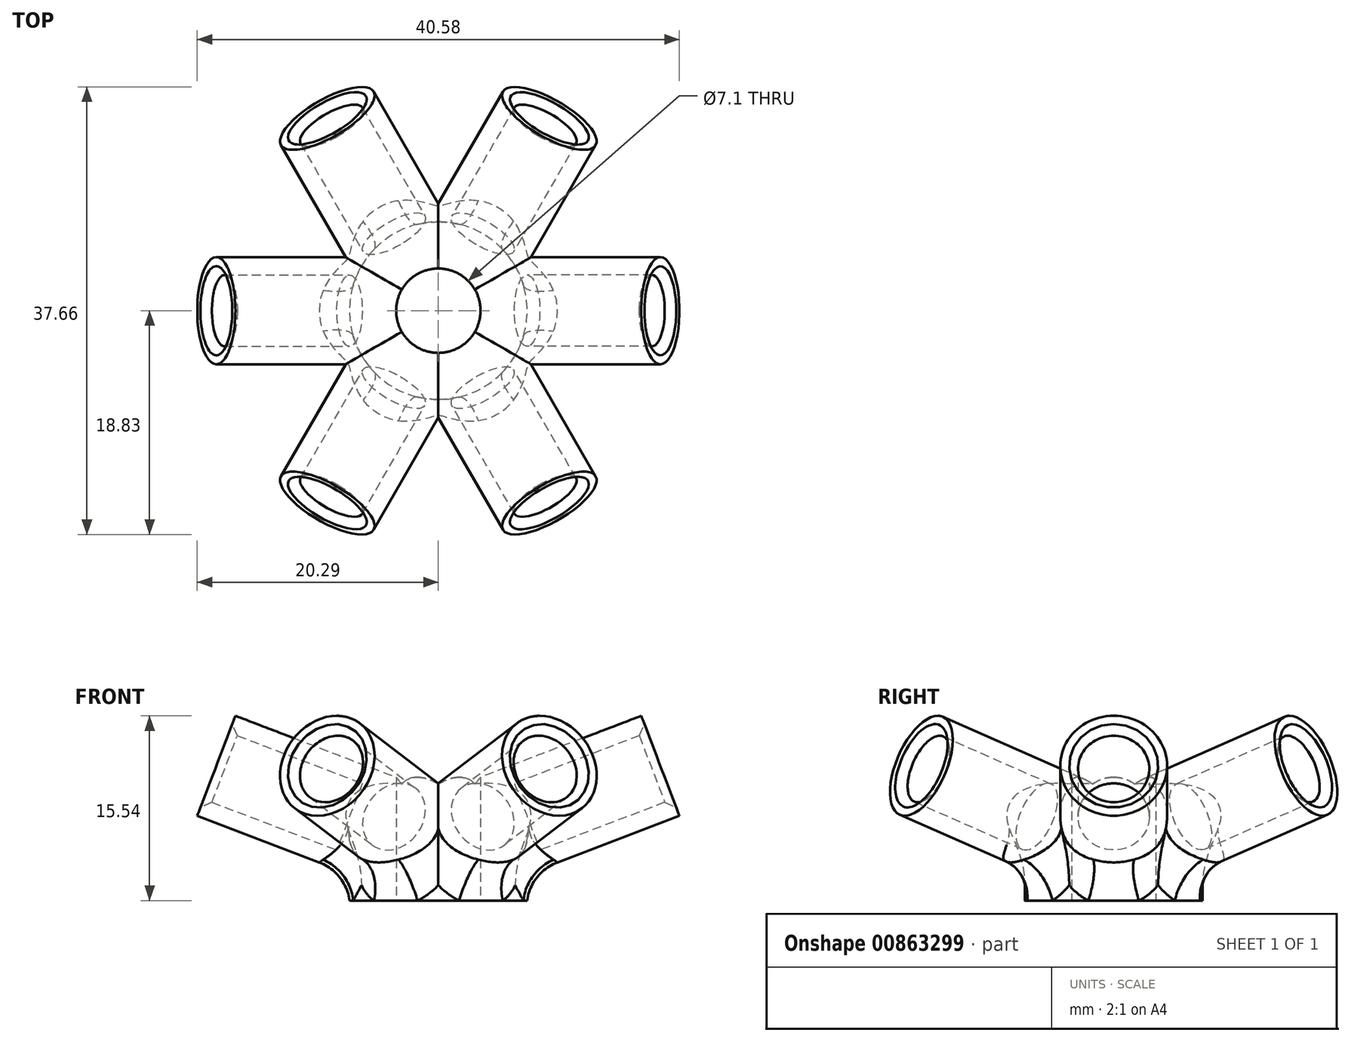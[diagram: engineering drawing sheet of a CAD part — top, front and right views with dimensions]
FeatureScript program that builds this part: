
annotation { "Feature Type Name" : "Feature", "Feature Type Description" : "" }
export const myFeature = defineFeature(function(context is Context, id is Id, definition is map)
    precondition{}
    {
        {
            assignVariable(context, id + "F0", {"name" : "espesor", "anyValue" : 1.5});
        }
        {
            var Q0;
            Q0=qCreatedBy(makeId("Front.planeOp"),FACE);
            var sketch = newSketch(context, id + "F1", { "sketchPlane" : qUnion([Q0])});
            skLineSegment(sketch, "E0", {"start": v(0, 0) * mm, "end": v(18.68, 7.14) * mm, "construction": true});
            skLineSegment(sketch, "E1", {"start": v(0, 0) * mm, "end": v(1.6, -4.2) * mm});
            skLineSegment(sketch, "E2", {"start": v(18.68, 7.14) * mm, "end": v(20.29, 2.93) * mm});
            skLineSegment(sketch, "E3", {"start": v(1.6, -4.2) * mm, "end": v(20.29, 2.93) * mm});
            skLineSegment(sketch, "E4", {"start": v(19.75, 4.33) * mm, "end": v(8.54, 0.05) * mm});
            skLineSegment(sketch, "E5", {"start": v(8.54, 0.05) * mm, "end": v(7.47, 2.85) * mm});
            skLineSegment(sketch, "E6", {"start": v(7.47, 2.85) * mm, "end": v(0, 0) * mm});
            skLineSegment(sketch, "E7", {"start": v(0, 0) * mm, "end": v(0, 41.35) * mm, "construction": true});
            skLineSegment(sketch, "E8", {"start": v(1.6, -4.2) * mm, "end": v(0, -4.2) * mm, "construction": true});
            skLineSegment(sketch, "E9", {"start": v(7.47, 2.85) * mm, "end": v(7.47, -4.2) * mm, "construction": true});
            skLineSegment(sketch, "E10", {"start": v(7.47, -4.2) * mm, "end": v(1.6, -4.2) * mm, "construction": true});
            skLineSegment(sketch, "E11", {"start": v(0, -4.2) * mm, "end": v(7.47, -4.2) * mm});
            skLineSegment(sketch, "E12", {"start": v(7.47, -4.2) * mm, "end": v(7.47, 2.85) * mm});
            skLineSegment(sketch, "E13", {"start": v(0, 2.85) * mm, "end": v(7.47, 2.85) * mm});
            skLineSegment(sketch, "E14", {"start": v(0, 2.85) * mm, "end": v(0, -4.2) * mm});
            skSolve(sketch);
        }
        {
            var Q0;
            {var subQ1=sQuery(id+"F1.wireOp",EDGE,"E4");Q0=makeQuery(id+"F1.imprint","IMPRINT",FACE,{"disambiguationData":[TD([[makeQuery(id+"F1.imprint","IMPRINT",EDGE,{"derivedFrom":subQ1}),1.0]])]});}
            var Q1;
            {var subQ0=sQuery(id+"F1.wireOp",EDGE,"E1");Q1=makeQuery(id+"F1.imprint","IMPRINT",FACE,{"disambiguationData":[TD([[makeQuery(id+"F1.imprint","IMPRINT",EDGE,{"derivedFrom":subQ0}),1.0]])]});}
            var Q2;
            Q2=sQuery(id+"F1.wireOp",EDGE,"E0");
            revolve(context, id + "F2", {"surfaceOperationType" : NewSurfaceOperationType.NEW, "entities" : qUnion([Q0, Q1]), "axis" : qUnion([Q2]), "revolveType" : RevolveType.FULL});
        }
        {
            var Q0;
            Q0=makeQuery(id+"F2.opRevolve","SWEPT_BODY",BODY,{"disambiguationData":[OSD([sQuery(id+"F1.wireOp",EDGE,"E1"),sQuery(id+"F1.wireOp",EDGE,"E2"),sQuery(id+"F1.wireOp",EDGE,"E3"),sQuery(id+"F1.wireOp",EDGE,"E4"),sQuery(id+"F1.wireOp",EDGE,"E5"),sQuery(id+"F1.wireOp",EDGE,"E6")])]});
            var Q1;
            Q1=sQuery(id+"F1.wireOp",EDGE,"E7");
            circularPattern(context, id + "F3", {"operationType" : NewBodyOperationType.ADD, "entities" : qUnion([Q0]), "axis" : qUnion([Q1]), "angle" : 360 * degree, "instanceCount" : 6, "equalSpace" : true});
        }
        {
            var Q0;
            {var subQ0=sQuery(id+"F1.wireOp",EDGE,"E1");Q0=makeQuery(id+"F1.imprint","IMPRINT",FACE,{"disambiguationData":[TD([[makeQuery(id+"F1.imprint","IMPRINT",EDGE,{"derivedFrom":subQ0}),-1.0]])]});}
            var Q1;
            {var subQ0=sQuery(id+"F1.wireOp",EDGE,"E1");Q1=makeQuery(id+"F1.imprint","IMPRINT",FACE,{"disambiguationData":[TD([[makeQuery(id+"F1.imprint","IMPRINT",EDGE,{"derivedFrom":subQ0}),1.0]])]});}
            var Q2;
            {var subQ0=sQuery(id+"F1.wireOp",EDGE,"E11");var subQ3=sQuery(id+"F1.wireOp",EDGE,"E12");var subQ5=makeQuery(id+"F1.imprint","INTERSECT",VERTEX,{"derivedFrom":[subQ0,subQ3]});Q2=makeQuery(id+"F1.imprint","IMPRINT",FACE,{"disambiguationData":[TD([[makeQuery(id+"F1.imprint","IMPRINT",EDGE,{"disambiguationData":[TD([[subQ5,-1.0]])],"derivedFrom":subQ3}),1.0]])]});}
            var Q3;
            {var subQ0=sQuery(id+"F1.wireOp",EDGE,"E6");Q3=makeQuery(id+"F1.imprint","IMPRINT",FACE,{"disambiguationData":[TD([[makeQuery(id+"F1.imprint","IMPRINT",EDGE,{"derivedFrom":subQ0}),-1.0]])]});}
            var Q4;
            Q4=sQuery(id+"F1.wireOp",EDGE,"E13");
            var Q5;
            Q5=sQuery(id+"F1.wireOp",EDGE,"E14");
            var Q6;
            Q6=sQuery(id+"F1.wireOp",EDGE,"E7");
            revolve(context, id + "F4", {"surfaceOperationType" : NewSurfaceOperationType.NEW, "entities" : qUnion([Q0, Q1, Q2, Q3]), "surfaceEntities" : qUnion([Q4, Q5]), "axis" : qUnion([Q6]), "revolveType" : RevolveType.FULL});
        }
        {
            var Q0;
            Q0=makeQuery(id+"F4.opRevolve","SWEPT_FACE",FACE,{"disambiguationData":[OSD([sQuery(id+"F1.wireOp",EDGE,"E11")])]});
            var sketch = newSketch(context, id + "F5", { "sketchPlane" : qUnion([Q0])});
            skCircle(sketch, "E15", {"center": v(0, 0) * mm, "radius": 3.55 * mm});
            skSolve(sketch);
        }
        {
            var Q0;
            Q0=makeQuery(id+"F5.imprint","IMPRINT",FACE,{"disambiguationData":[TD([[makeQuery(id+"F5.imprint","IMPRINT",EDGE,{"derivedFrom":sQuery(id+"F5.wireOp",EDGE,"E15")}),1.0]])]});
            extrude(context, id + "F6", {"entities" : qUnion([Q0]), "operationType" : NewBodyOperationType.REMOVE, "endBound" : BoundingType.THROUGH_ALL, "oppositeDirection" : true, "depth" : 25 * mm, "offsetDistance" : 25 * mm});
        }
        {
            var Q0;
            Q0=makeQuery(id+"F2.opRevolve","SWEPT_BODY",BODY,{"disambiguationData":[OSD([sQuery(id+"F1.wireOp",EDGE,"E1"),sQuery(id+"F1.wireOp",EDGE,"E2"),sQuery(id+"F1.wireOp",EDGE,"E3"),sQuery(id+"F1.wireOp",EDGE,"E4"),sQuery(id+"F1.wireOp",EDGE,"E5"),sQuery(id+"F1.wireOp",EDGE,"E6")])]});
            var Q1;
            Q1=makeQuery(id+"F4.opRevolve","SWEPT_BODY",BODY,{"disambiguationData":[OSD([sQuery(id+"F1.wireOp",EDGE,"E11"),sQuery(id+"F1.wireOp",EDGE,"E12"),sQuery(id+"F1.wireOp",EDGE,"E13"),sQuery(id+"F1.wireOp",EDGE,"E14")])]});
            booleanBodies(context, id + "F7", {"operationType" : BooleanOperationType.UNION, "tools" : qUnion([Q0, Q1])});
        }
        {
            var Q0;
            {var subQ0=makeQuery(id+"F2.opRevolve","SWEPT_FACE",FACE,{"disambiguationData":[OSD([sQuery(id+"F1.wireOp",EDGE,"E1")])]});var subQ1=makeQuery(id+"F2.opRevolve","SWEPT_FACE",FACE,{"disambiguationData":[OSD([sQuery(id+"F1.wireOp",EDGE,"E3")])]});Q0=makeQuery(id+"F7.opBoolean","INTERSECT",EDGE,{"derivedFrom":[makeQuery(id+"F4.opRevolve","SWEPT_FACE",FACE,{"disambiguationData":[OSD([sQuery(id+"F1.wireOp",EDGE,"E12")])]}),makeQuery(id+"F3.boolean.opBoolean","SPLIT",FACE,{"disambiguationData":[TD([subQ0])],"derivedFrom":makeQuery(id+"F3.opPattern","COPY",FACE,{"derivedFrom":subQ1,"instanceName":"1"})})]});}
            var Q1;
            {var subQ0=makeQuery(id+"F2.opRevolve","SWEPT_FACE",FACE,{"disambiguationData":[OSD([sQuery(id+"F1.wireOp",EDGE,"E3")])]});Q1=makeQuery(id+"F7.opBoolean","INTERSECT",EDGE,{"derivedFrom":[makeQuery(id+"F4.opRevolve","SWEPT_FACE",FACE,{"disambiguationData":[OSD([sQuery(id+"F1.wireOp",EDGE,"E12")])]}),makeQuery(id+"F3.boolean.opBoolean","SPLIT",FACE,{"disambiguationData":[TD([subQ0])],"derivedFrom":makeQuery(id+"F3.opPattern","COPY",FACE,{"derivedFrom":subQ0,"instanceName":"2"})})]});}
            var Q2;
            {var subQ0=makeQuery(id+"F2.opRevolve","SWEPT_FACE",FACE,{"disambiguationData":[OSD([sQuery(id+"F1.wireOp",EDGE,"E3")])]});var subQ1=makeQuery(id+"F2.opRevolve","SWEPT_FACE",FACE,{"disambiguationData":[OSD([sQuery(id+"F1.wireOp",EDGE,"E1")])]});Q2=makeQuery(id+"F7.opBoolean","INTERSECT",EDGE,{"derivedFrom":[makeQuery(id+"F4.opRevolve","SWEPT_FACE",FACE,{"disambiguationData":[OSD([sQuery(id+"F1.wireOp",EDGE,"E12")])]}),makeQuery(id+"F3.boolean.opBoolean","SPLIT",FACE,{"disambiguationData":[TD([subQ1])],"derivedFrom":subQ0})]});}
            var Q3;
            {var subQ0=makeQuery(id+"F2.opRevolve","SWEPT_FACE",FACE,{"disambiguationData":[OSD([sQuery(id+"F1.wireOp",EDGE,"E3")])]});var subQ1=makeQuery(id+"F2.opRevolve","SWEPT_FACE",FACE,{"disambiguationData":[OSD([sQuery(id+"F1.wireOp",EDGE,"E1")])]});Q3=makeQuery(id+"F7.opBoolean","INTERSECT",EDGE,{"derivedFrom":[makeQuery(id+"F4.opRevolve","SWEPT_FACE",FACE,{"disambiguationData":[OSD([sQuery(id+"F1.wireOp",EDGE,"E12")])]}),makeQuery(id+"F3.boolean.opBoolean","SPLIT",FACE,{"disambiguationData":[TD([subQ1])],"derivedFrom":makeQuery(id+"F3.opPattern","COPY",FACE,{"derivedFrom":subQ0,"instanceName":"5"})})]});}
            var Q4;
            {var subQ1=makeQuery(id+"F2.opRevolve","SWEPT_FACE",FACE,{"disambiguationData":[OSD([sQuery(id+"F1.wireOp",EDGE,"E3")])]});Q4=makeQuery(id+"F7.opBoolean","INTERSECT",EDGE,{"derivedFrom":[makeQuery(id+"F4.opRevolve","SWEPT_FACE",FACE,{"disambiguationData":[OSD([sQuery(id+"F1.wireOp",EDGE,"E12")])]}),makeQuery(id+"F3.boolean.opBoolean","SPLIT",FACE,{"disambiguationData":[TD([subQ1])],"derivedFrom":makeQuery(id+"F3.opPattern","COPY",FACE,{"derivedFrom":subQ1,"instanceName":"4"})})]});}
            var Q5;
            {var subQ1=makeQuery(id+"F2.opRevolve","SWEPT_FACE",FACE,{"disambiguationData":[OSD([sQuery(id+"F1.wireOp",EDGE,"E3")])]});Q5=makeQuery(id+"F7.opBoolean","INTERSECT",EDGE,{"derivedFrom":[makeQuery(id+"F4.opRevolve","SWEPT_FACE",FACE,{"disambiguationData":[OSD([sQuery(id+"F1.wireOp",EDGE,"E12")])]}),makeQuery(id+"F3.boolean.opBoolean","SPLIT",FACE,{"disambiguationData":[TD([subQ1])],"derivedFrom":makeQuery(id+"F3.opPattern","COPY",FACE,{"derivedFrom":subQ1,"instanceName":"3"})})]});}
            fillet(context, id + "F8", {"entities" : qUnion([Q0, Q1, Q2, Q3, Q4, Q5]), "radius" : 4 * mm, "tangentPropagation" : true, "allowEdgeOverflow" : false});
        }
        {
            var Q0;
            Q0=makeQuery(id+"F3.opPattern","COPY",EDGE,{"derivedFrom":makeQuery(id+"F2.opRevolve","SWEPT_EDGE",EDGE,{"disambiguationData":[OSD([sQuery(id+"F1.wireOp",EDGE,"E2"),sQuery(id+"F1.wireOp",EDGE,"E4")])]}),"instanceName":"5"});
            var Q1;
            Q1=makeQuery(id+"F3.opPattern","COPY",EDGE,{"derivedFrom":makeQuery(id+"F2.opRevolve","SWEPT_EDGE",EDGE,{"disambiguationData":[OSD([sQuery(id+"F1.wireOp",EDGE,"E2"),sQuery(id+"F1.wireOp",EDGE,"E4")])]}),"instanceName":"4"});
            var Q2;
            Q2=makeQuery(id+"F2.opRevolve","SWEPT_EDGE",EDGE,{"disambiguationData":[OSD([sQuery(id+"F1.wireOp",EDGE,"E2"),sQuery(id+"F1.wireOp",EDGE,"E4")])]});
            var Q3;
            Q3=makeQuery(id+"F3.opPattern","COPY",EDGE,{"derivedFrom":makeQuery(id+"F2.opRevolve","SWEPT_EDGE",EDGE,{"disambiguationData":[OSD([sQuery(id+"F1.wireOp",EDGE,"E2"),sQuery(id+"F1.wireOp",EDGE,"E4")])]}),"instanceName":"1"});
            var Q4;
            Q4=makeQuery(id+"F3.opPattern","COPY",EDGE,{"derivedFrom":makeQuery(id+"F2.opRevolve","SWEPT_EDGE",EDGE,{"disambiguationData":[OSD([sQuery(id+"F1.wireOp",EDGE,"E2"),sQuery(id+"F1.wireOp",EDGE,"E4")])]}),"instanceName":"2"});
            var Q5;
            Q5=makeQuery(id+"F3.opPattern","COPY",EDGE,{"derivedFrom":makeQuery(id+"F2.opRevolve","SWEPT_EDGE",EDGE,{"disambiguationData":[OSD([sQuery(id+"F1.wireOp",EDGE,"E2"),sQuery(id+"F1.wireOp",EDGE,"E4")])]}),"instanceName":"3"});
            chamfer(context, id + "F9", {"entities" : qUnion([Q0, Q1, Q2, Q3, Q4, Q5]), "width" : (getVariable(context, 'espesor') / 2) * mm, "tangentPropagation" : true});
        }
    });
